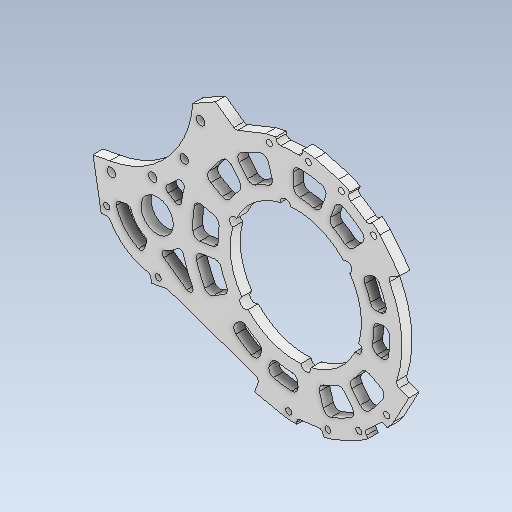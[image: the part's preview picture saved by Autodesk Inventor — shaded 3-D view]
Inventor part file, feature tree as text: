
AUTODESK INVENTOR PART (.ipt)
format: ipt  version: 2020 (Build 240168000, 168)  size: 1,084,416 bytes
history: native  units: mm
features: reference x21, sketch x12, extrude x11, other x10, projected_geometry x8, fillet x6, shell x4, hole x1, chamfer x1, thicken_offset x1, pattern_circular x1
ambient origin geometry x8: Origin, YZ Plane, XZ Plane, XY Plane, X Axis, Y Axis, Z Axis, Center Point
bodies: Solid1 (feature_tree)
feature tree (76):
  extrude  "Extrusion1"  Depth=45.0mm
  extrude  "Extrusion2"  Depth=5.0mm TaperAngle=0.0deg
  hole  "Hole1"  [1 undecoded]
  extrude  "Extrusion4"  Depth=2.0mm TaperAngle=45.0deg
  chamfer  "Chamfer1"  Distance=5.0mm
  extrude  "Extrusion5"  Depth=118.0mm
  extrude  "Extrusion6"  Depth=40.0mm
  extrude  "Extrusion8"  Depth=5.0mm
  extrude  "Extrusion9"  Depth=77.0mm
  extrude  "Extrusion10"  TaperAngle=60.0deg  [1 undecoded]
  thicken_offset  "Thicken1"
  extrude  "Extrusion11"  Depth=2.0mm TaperAngle=360.0deg
  fillet  "Fillet1"  Radius=5.0mm
  fillet  "Fillet2"  Radius=5.0mm
  extrude  "Extrusion12"  Depth=5.0mm
  fillet  "Fillet3"  Radius=5.0mm
  fillet  "Fillet4"  Radius=5.0mm
  fillet  "Fillet5"  Radius=5.0mm
  extrude  "Extrusion13"  Depth=5.0mm
  pattern_circular  "Circular Pattern1"  [2 undecoded]
  fillet  "Fillet6"  Radius=25.0mm
  sketch  "Sketch1"  dims[d0=100.0mm d1=45.0mm]
  reference  "Reference1"
  reference  "Reference2"
  reference  "Reference3"
  reference  "Reference4"
  reference  "Reference5"
  reference  "Reference6"
  sketch  "Sketch2"  dims[d2=105.0mm d3=5.0mm d4=0.0mm]
  projected_geometry  "Projected Loop1"
  sketch  "Sketch3"  dims[d5=5.0mm d6=0.0mm]
  reference  "Reference7"
  reference  "Reference8"
  reference  "Reference9"
  reference  "Reference10"
  reference  "Reference11"
  reference  "Reference12"
  reference  "Reference13"
  reference  "Reference14"
  reference  "Reference15"
  reference  "Reference16"
  sketch  "Sketch6"  dims[d7=3.0mm d8=6.0mm d9=4.0mm d10=2.0mm d11=90.0deg d12=17.0mm d13=0.0mm d16=65.0mm]
  reference  "Reference17"
  reference  "Reference18"
  sketch  "Sketch7"  dims[d17=5.0mm d18=0.0mm d19=15.0mm d20=2.0mm d21=45.0deg]
  reference  "Reference19"
  sketch  "Sketch8"  dims[d22=16.0mm d23=5.0mm d24=0.0mm]
  projected_geometry  "Projected Loop4"
  sketch  "Sketch10"  dims[d25=100.0mm d26=118.0mm]
  reference  "Reference22"
  projected_geometry  "Projected Loop5"
  sketch  "Sketch11"  dims[d27=4.2mm d28=40.0mm d30=12.217305mm]
  projected_geometry  "Projected Loop6"
  sketch  "Sketch12"  dims[d32=5.0mm d33=0.0mm d38=65.0mm]
  reference  "Reference23"
  projected_geometry  "Projected Loop7"
  sketch  "Sketch13"  dims[d39=77.0mm d40=93.0mm]
  projected_geometry  "Projected Loop8"
  sketch  "Sketch14"  dims[d41=102.0mm d42=60.0deg]
  projected_geometry  "Projected Loop9"
  sketch  "Sketch15"  dims[d43=15.0deg d44=60.0mm d46=360.0deg d48=5.0mm d49=0.0mm d50=5.0mm d51=5.0mm d52=5.0mm d53=5.0mm d54=5.0mm d55=5.0mm d56=5.0mm d57=0.0mm d58=25.0mm d59=42.0mm d60=60.0deg d61=5.0mm d62=0.0mm d63=1.0mm d64=1.0mm d65=27.0mm d66=115.0mm d67=5.0mm d68=0.0mm d69=2.0mm d70=2.0mm d71=27.0mm d72=117.0mm d73=114.0mm d74=5.0mm d75=0.0mm d76=2.0mm d77=3.0mm d78=3.0mm d79=5.0mm d80=5.0mm d81=0.0mm d82=60.0mm d83=360.0deg d85=2.0mm]
  projected_geometry  "Projected Loop10"
  parser-record x1  (decoder bookkeeping rows leaked as tree rows — omitted from the tree; the rows remain in map.json)
  other  "reducer_2.iam"
  shell  "shell_2:3"  Thickness=42.0mm
  shell  "shell_2:4"  Thickness=60.0deg
  shell  "shell_2:1"  Thickness=5.0mm
  other  "90_motor:1"
  other  "90motor_top:1"
  shell  "shell_3:1"  Thickness=1.0mm
  other  "motor_h_1:1"
  other  "xl_60_out_2:1"
  other  "bearing_6810zz:1"
  other  "xl_wheel_ass:1"
  other  "xl_20_ori:1"
  other  "motor_h_3:1"
note: 4 required parameter values undecoded (feature->parameter linkage not recoverable at this tier; creation-order binding heuristic only, values carry confidence <= 0.55)
note: 1 file-system path scrubbed to <path> (originals preserved in map.json)
